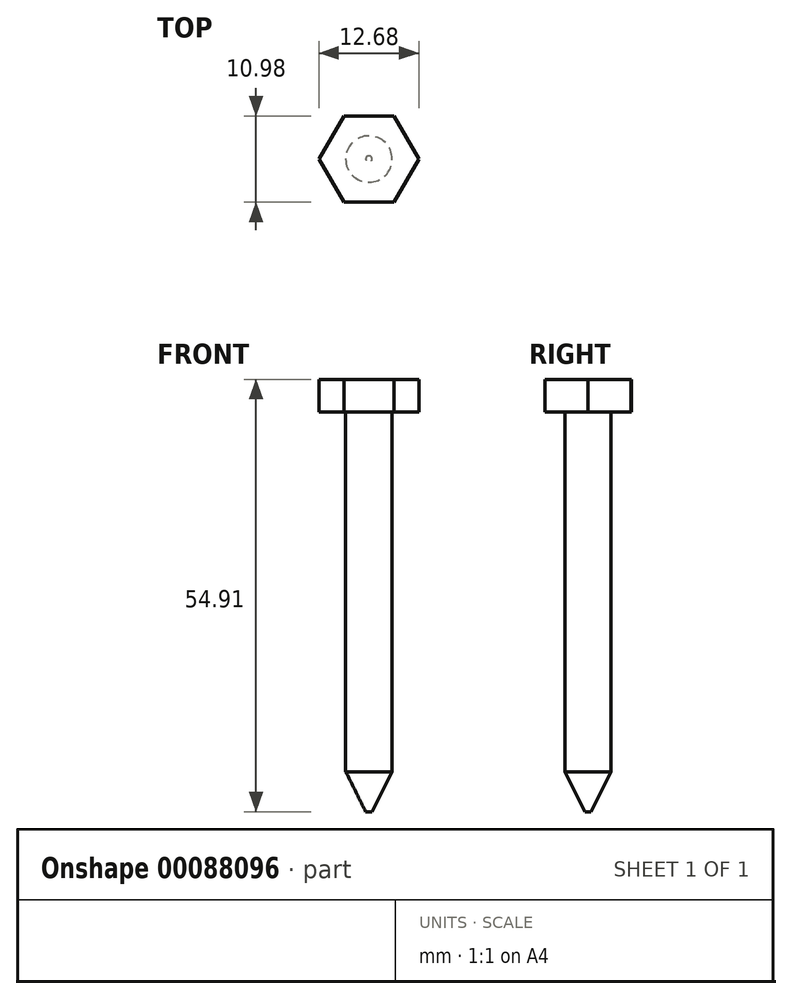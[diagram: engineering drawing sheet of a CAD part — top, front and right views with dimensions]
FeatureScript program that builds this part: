
annotation { "Feature Type Name" : "Feature", "Feature Type Description" : "" }
export const myFeature = defineFeature(function(context is Context, id is Id, definition is map)
    precondition{}
    {
        {
            var Q0;
            Q0=qCreatedBy(makeId("Top.planeOp"),FACE);
            var sketch = newSketch(context, id + "F0", { "sketchPlane" : qUnion([Q0])});
            skCircle(sketch, "E0.cCircle", {"center": v(0, 0) * mm, "radius": 5.49 * mm, "construction": true});
            skLineSegment(sketch, "E0.0", {"start": v(6.34, 0) * mm, "end": v(3.16, -5.5) * mm});
            skLineSegment(sketch, "E0.1", {"start": v(3.16, -5.5) * mm, "end": v(-3.18, -5.48) * mm});
            skLineSegment(sketch, "E0.2", {"start": v(-3.18, -5.48) * mm, "end": v(-6.34, 0) * mm});
            skLineSegment(sketch, "E0.3", {"start": v(-6.34, 0) * mm, "end": v(-3.16, 5.5) * mm});
            skLineSegment(sketch, "E0.4", {"start": v(-3.16, 5.5) * mm, "end": v(3.18, 5.48) * mm});
            skLineSegment(sketch, "E0.5", {"start": v(3.18, 5.48) * mm, "end": v(6.34, 0) * mm});
            skPoint(sketch, "E0.0.midPoint", {"position": v(4.75, -2.75) * mm});
            skSolve(sketch);
        }
        {
            var Q0;
            Q0=makeQuery(id+"F0.imprint","IMPRINT",FACE,{"disambiguationData":[TD([[makeQuery(id+"F0.imprint","IMPRINT",EDGE,{"derivedFrom":sQuery(id+"F0.wireOp",EDGE,"E0.0")}),-1.0]])]});
            extrude(context, id + "F1", {"entities" : qUnion([Q0]), "depth" : 4.11 * mm});
        }
        {
            var Q0;
            Q0=makeQuery(id+"F1.opExtrude","CAP_FACE",FACE,{"disambiguationData":[OSD([sQuery(id+"F0.wireOp",EDGE,"E0.0"),sQuery(id+"F0.wireOp",EDGE,"E0.1"),sQuery(id+"F0.wireOp",EDGE,"E0.2"),sQuery(id+"F0.wireOp",EDGE,"E0.3"),sQuery(id+"F0.wireOp",EDGE,"E0.4"),sQuery(id+"F0.wireOp",EDGE,"E0.5")])],"isStart":true});
            var sketch = newSketch(context, id + "F2", { "sketchPlane" : qUnion([Q0])});
            skCircle(sketch, "E1", {"center": v(0, 0) * mm, "radius": 2.95 * mm});
            skSolve(sketch);
        }
        {
            var Q0;
            Q0=makeQuery(id+"F2.imprint","IMPRINT",FACE,{"disambiguationData":[TD([[makeQuery(id+"F2.imprint","IMPRINT",EDGE,{"derivedFrom":sQuery(id+"F2.wireOp",EDGE,"E1")}),1.0]])]});
            extrude(context, id + "F3", {"entities" : qUnion([Q0]), "operationType" : NewBodyOperationType.ADD, "depth" : 50.8 * mm});
        }
        {
            var Q0;
            Q0=makeQuery(id+"F3.opExtrude","CAP_EDGE",EDGE,{"disambiguationData":[OSD([sQuery(id+"F2.wireOp",EDGE,"E1")])],"isStart":false});
            chamfer(context, id + "F4", {"entities" : qUnion([Q0]), "chamferType" : ChamferType.TWO_OFFSETS, "width1" : 2.54 * mm, "oppositeDirection" : false, "width2" : 5.08 * mm, "tangentPropagation" : true});
        }
    });
